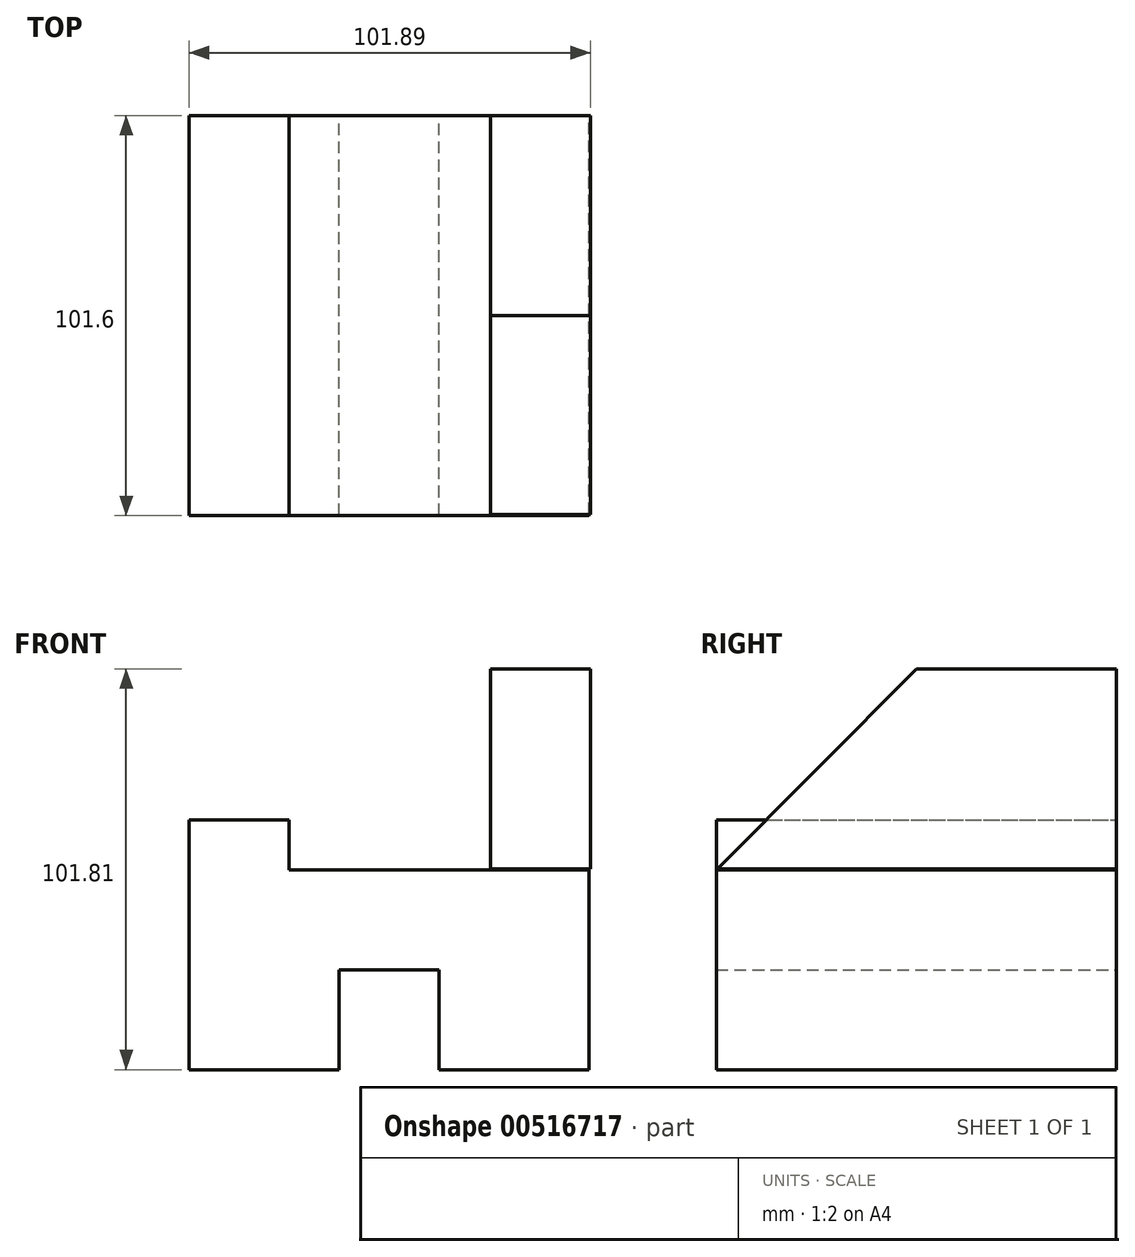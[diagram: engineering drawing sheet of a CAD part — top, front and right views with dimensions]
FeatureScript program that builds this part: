
annotation { "Feature Type Name" : "Feature", "Feature Type Description" : "" }
export const myFeature = defineFeature(function(context is Context, id is Id, definition is map)
    precondition{}
    {
        {
            var Q0;
            Q0=qCreatedBy(makeId("Front.planeOp"),FACE);
            var sketch = newSketch(context, id + "F0", { "sketchPlane" : qUnion([Q0])});
            skLineSegment(sketch, "E0", {"start": v(55.84, -25.4) * mm, "end": v(55.84, 25.4) * mm});
            skLineSegment(sketch, "E1", {"start": v(55.84, -25.4) * mm, "end": v(17.74, -25.4) * mm});
            skLineSegment(sketch, "E2", {"start": v(17.74, -25.4) * mm, "end": v(17.74, 0) * mm});
            skLineSegment(sketch, "E3", {"start": v(17.74, 0) * mm, "end": v(-7.66, 0) * mm});
            skLineSegment(sketch, "E4", {"start": v(-7.66, 0) * mm, "end": v(-7.66, -25.4) * mm});
            skLineSegment(sketch, "E5", {"start": v(-7.66, -25.4) * mm, "end": v(-45.76, -25.4) * mm});
            skLineSegment(sketch, "E6", {"start": v(-45.76, -25.4) * mm, "end": v(-45.76, 38.1) * mm});
            skLineSegment(sketch, "E7", {"start": v(-20.36, 38.1) * mm, "end": v(-45.76, 38.1) * mm});
            skLineSegment(sketch, "E8", {"start": v(-20.36, 38.1) * mm, "end": v(-20.36, 25.4) * mm});
            skLineSegment(sketch, "E9", {"start": v(55.84, 25.4) * mm, "end": v(-20.36, 25.4) * mm});
            skSolve(sketch);
        }
        {
            var Q0;
            Q0=makeQuery(id+"F0.imprint","IMPRINT",FACE,{"disambiguationData":[TD([[makeQuery(id+"F0.imprint","IMPRINT",EDGE,{"derivedFrom":sQuery(id+"F0.wireOp",EDGE,"E0")}),1.0]])]});
            extrude(context, id + "F1", {"entities" : qUnion([Q0]), "depth" : 101.6 * mm, "offsetDistance" : 25.4 * mm});
        }
        {
            var Q0;
            Q0=qCreatedBy(makeId("Right.planeOp"),FACE);
            var sketch = newSketch(context, id + "F2", { "sketchPlane" : qUnion([Q0])});
            skLineSegment(sketch, "E10", {"start": v(0, 25.61) * mm, "end": v(0, 76.41) * mm});
            skLineSegment(sketch, "E11", {"start": v(0, 76.41) * mm, "end": v(-50.8, 76.41) * mm});
            skLineSegment(sketch, "E12", {"start": v(-50.8, 76.41) * mm, "end": v(-101.34, 25.61) * mm});
            skLineSegment(sketch, "E13", {"start": v(-101.34, 25.61) * mm, "end": v(0, 25.61) * mm});
            skSolve(sketch);
        }
        {
            var Q0;
            Q0=makeQuery(id+"F2.imprint","IMPRINT",FACE,{"disambiguationData":[TD([[makeQuery(id+"F2.imprint","IMPRINT",EDGE,{"derivedFrom":sQuery(id+"F2.wireOp",EDGE,"E10")}),1.0]])]});
            extrude(context, id + "F3", {"entities" : qUnion([Q0]), "depth" : 56.13 * mm, "offsetDistance" : 25.4 * mm});
        }
        {
            var Q0;
            Q0=makeQuery(id+"F3.opExtrude","CAP_FACE",FACE,{"disambiguationData":[OSD([sQuery(id+"F2.wireOp",EDGE,"E10"),sQuery(id+"F2.wireOp",EDGE,"E11"),sQuery(id+"F2.wireOp",EDGE,"E12"),sQuery(id+"F2.wireOp",EDGE,"E13")])],"isStart":true});
            extrude(context, id + "F4", {"entities" : qUnion([Q0]), "operationType" : NewBodyOperationType.REMOVE, "oppositeDirection" : true, "depth" : 30.73 * mm, "offsetDistance" : 25.4 * mm});
        }
    });
